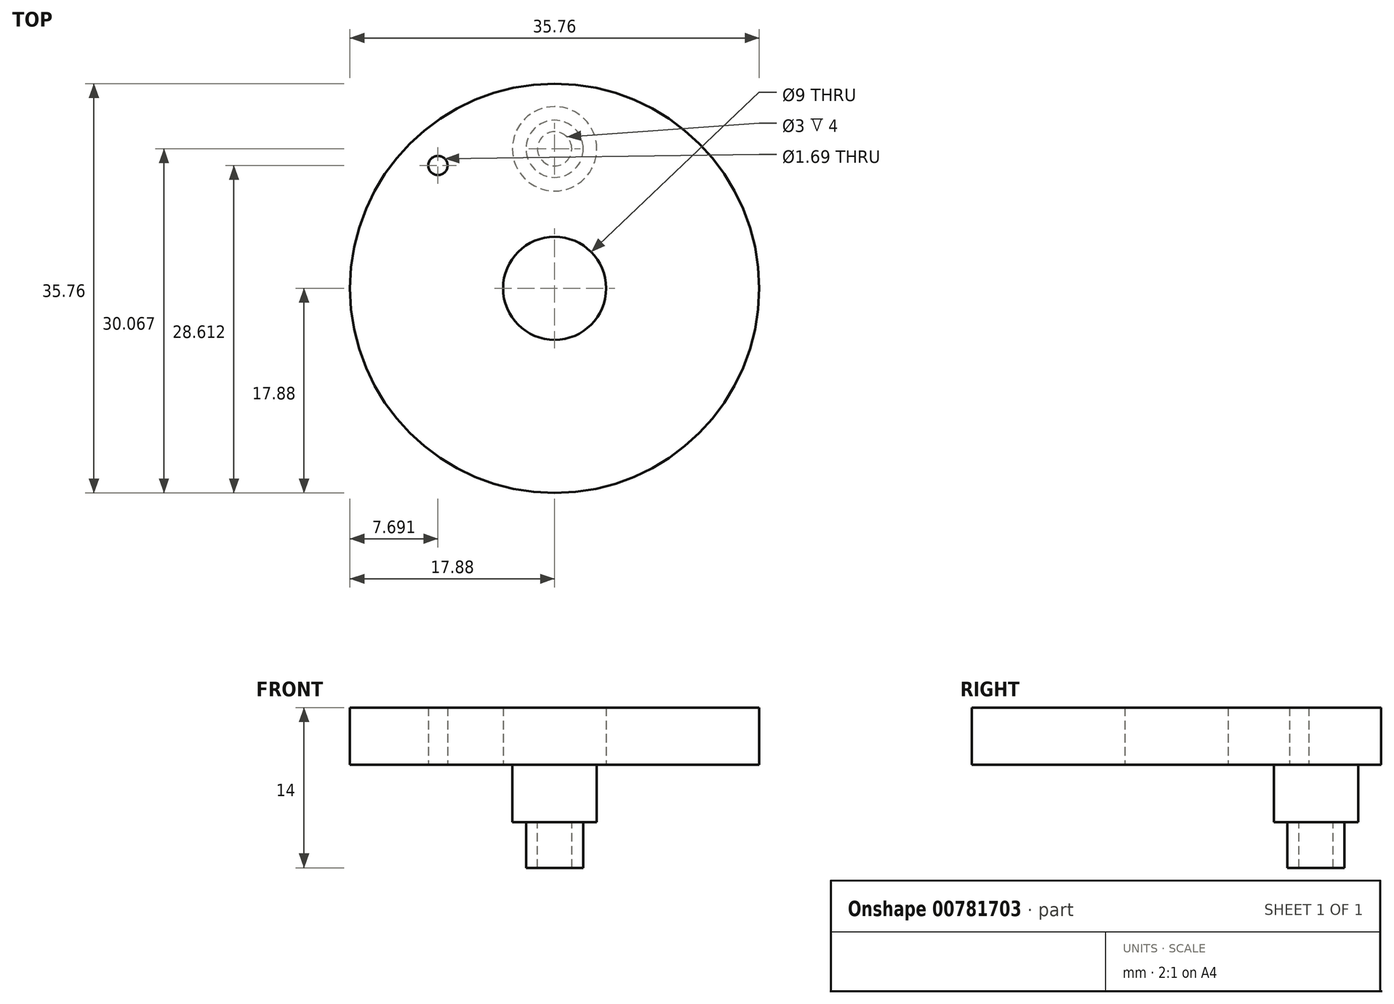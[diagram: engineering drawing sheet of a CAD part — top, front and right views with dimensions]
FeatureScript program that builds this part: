
annotation { "Feature Type Name" : "Feature", "Feature Type Description" : "" }
export const myFeature = defineFeature(function(context is Context, id is Id, definition is map)
    precondition{}
    {
        {
            var Q0;
            Q0=qCreatedBy(makeId("Top.planeOp"),FACE);
            var sketch = newSketch(context, id + "F0", { "sketchPlane" : qUnion([Q0])});
            skCircle(sketch, "E0", {"center": v(0, 0) * mm, "radius": 17.88 * mm});
            skCircle(sketch, "E1", {"center": v(0, 0) * mm, "radius": 4.5 * mm});
            skSolve(sketch);
        }
        {
            var Q0;
            Q0=makeQuery(id+"F0.imprint","IMPRINT",FACE,{"disambiguationData":[TD([[makeQuery(id+"F0.imprint","IMPRINT",EDGE,{"derivedFrom":sQuery(id+"F0.wireOp",EDGE,"E0")}),1.0]])]});
            extrude(context, id + "F1", {"entities" : qUnion([Q0]), "depth" : 5 * mm, "offsetDistance" : 25.4 * mm});
        }
        {
            var Q0;
            Q0=makeQuery(id+"F1.opExtrude","CAP_FACE",FACE,{"disambiguationData":[OSD([sQuery(id+"F0.wireOp",EDGE,"E0"),sQuery(id+"F0.wireOp",EDGE,"E1")])],"isStart":false});
            var sketch = newSketch(context, id + "F2", { "sketchPlane" : qUnion([Q0])});
            skCircle(sketch, "E2", {"center": v(0, 12.19) * mm, "radius": 3.69 * mm});
            skSolve(sketch);
        }
        {
            var Q0;
            Q0=makeQuery(id+"F2.imprint","IMPRINT",FACE,{"disambiguationData":[TD([[makeQuery(id+"F2.imprint","IMPRINT",EDGE,{"derivedFrom":sQuery(id+"F2.wireOp",EDGE,"E2")}),1.0]])]});
            extrude(context, id + "F3", {"entities" : qUnion([Q0]), "operationType" : NewBodyOperationType.ADD, "oppositeDirection" : true, "depth" : 10 * mm, "offsetDistance" : 25.4 * mm});
        }
        {
            var Q0;
            Q0=makeQuery(id+"F3.opExtrude","CAP_FACE",FACE,{"disambiguationData":[OSD([sQuery(id+"F2.wireOp",EDGE,"E2")])],"isStart":false});
            var sketch = newSketch(context, id + "F4", { "sketchPlane" : qUnion([Q0])});
            skCircle(sketch, "E3", {"center": v(0, -12.19) * mm, "radius": 2.5 * mm});
            skCircle(sketch, "E4", {"center": v(0, -12.19) * mm, "radius": 1.5 * mm});
            skSolve(sketch);
        }
        {
            var Q0;
            Q0=makeQuery(id+"F4.imprint","IMPRINT",FACE,{"disambiguationData":[TD([[makeQuery(id+"F4.imprint","IMPRINT",EDGE,{"derivedFrom":sQuery(id+"F4.wireOp",EDGE,"E3")}),1.0]])]});
            extrude(context, id + "F5", {"entities" : qUnion([Q0]), "operationType" : NewBodyOperationType.ADD, "depth" : 4 * mm, "offsetDistance" : 25.4 * mm});
        }
        {
            var Q0;
            Q0=qCreatedBy(makeId("Top.planeOp"),FACE);
            var sketch = newSketch(context, id + "F6", { "sketchPlane" : qUnion([Q0])});
            skCircle(sketch, "E5", {"center": v(-10.19, 10.73) * mm, "radius": 0.84 * mm});
            skSolve(sketch);
        }
        {
            var Q0;
            Q0 = qSketchRegion(id + "F6", true);
            extrude(context, id + "F7", {"entities" : qUnion([Q0]), "operationType" : NewBodyOperationType.REMOVE, "depth" : 25 * mm, "offsetDistance" : 25 * mm});
        }
    });
